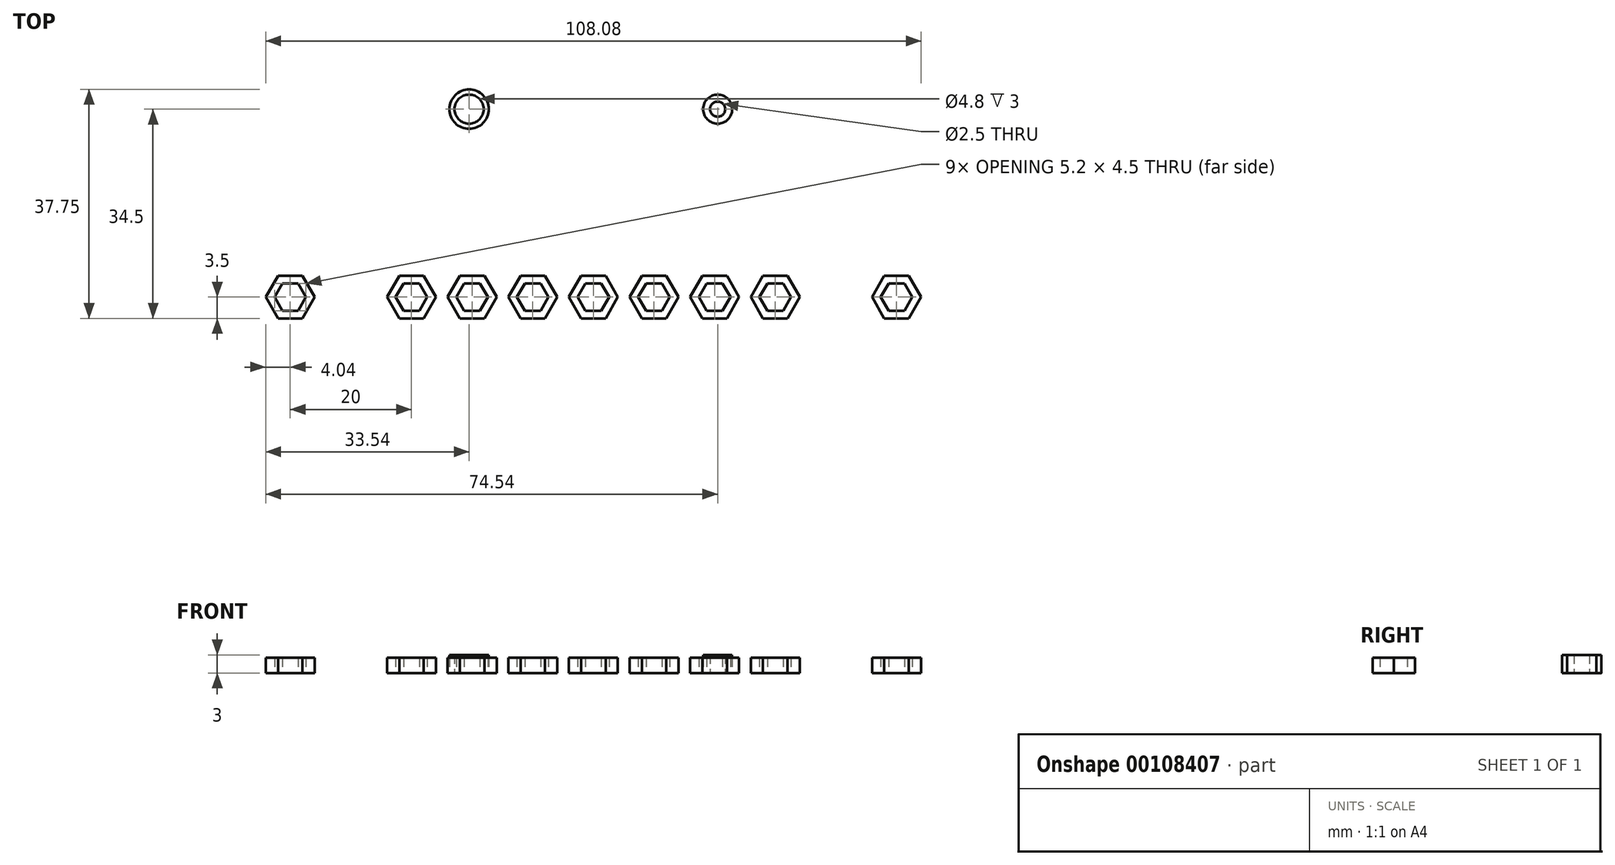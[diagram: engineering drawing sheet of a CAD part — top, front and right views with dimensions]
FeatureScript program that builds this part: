
annotation { "Feature Type Name" : "Feature", "Feature Type Description" : "" }
export const myFeature = defineFeature(function(context is Context, id is Id, definition is map)
    precondition{}
    {
        {
            var Q0;
            Q0=qCreatedBy(makeId("Top.planeOp"),FACE);
            var sketch = newSketch(context, id + "F0", { "sketchPlane" : qUnion([Q0])});
            skLineSegment(sketch, "E0.bottom", {"start": v(-57, 22.5) * mm, "end": v(57, 22.5) * mm});
            skLineSegment(sketch, "E0.top", {"start": v(-57, -22.5) * mm, "end": v(57, -22.5) * mm});
            skLineSegment(sketch, "E0.left", {"start": v(-57, 22.5) * mm, "end": v(-57, -22.5) * mm});
            skLineSegment(sketch, "E0.right", {"start": v(57, 22.5) * mm, "end": v(57, -22.5) * mm});
            skPoint(sketch, "E0.middle", {"position": v(0, 0) * mm});
            skLineSegment(sketch, "E1", {"start": v(57, -22.5) * mm, "end": v(57, -12.5) * mm});
            skLineSegment(sketch, "E2", {"start": v(-57, -22.5) * mm, "end": v(-57, -12.5) * mm});
            skLineSegment(sketch, "E3", {"start": v(0, -22.5) * mm, "end": v(0, -16) * mm});
            skCircle(sketch, "E4.cCircle", {"center": v(0, -16) * mm, "radius": 3.5 * mm, "construction": true});
            skLineSegment(sketch, "E4.0", {"start": v(-2.02, -12.5) * mm, "end": v(2.02, -12.5) * mm});
            skLineSegment(sketch, "E4.1", {"start": v(2.02, -12.5) * mm, "end": v(4.04, -16) * mm});
            skLineSegment(sketch, "E4.2", {"start": v(4.04, -16) * mm, "end": v(2.02, -19.5) * mm});
            skLineSegment(sketch, "E4.3", {"start": v(2.02, -19.5) * mm, "end": v(-2.02, -19.5) * mm});
            skLineSegment(sketch, "E4.4", {"start": v(-2.02, -19.5) * mm, "end": v(-4.04, -16) * mm});
            skLineSegment(sketch, "E4.5", {"start": v(-4.04, -16) * mm, "end": v(-2.02, -12.5) * mm});
            skPoint(sketch, "E4.0.midPoint", {"position": v(0, -12.5) * mm});
            skLineSegment(sketch, "E5", {"start": v(0, -19.5) * mm, "end": v(0, -18.25) * mm});
            skCircle(sketch, "E6.cCircle", {"center": v(0, -16) * mm, "radius": 2.25 * mm, "construction": true});
            skLineSegment(sketch, "E6.0", {"start": v(1.3, -18.25) * mm, "end": v(-1.3, -18.25) * mm});
            skLineSegment(sketch, "E6.1", {"start": v(-1.3, -18.25) * mm, "end": v(-2.6, -16) * mm});
            skLineSegment(sketch, "E6.2", {"start": v(-2.6, -16) * mm, "end": v(-1.3, -13.75) * mm});
            skLineSegment(sketch, "E6.3", {"start": v(-1.3, -13.75) * mm, "end": v(1.3, -13.75) * mm});
            skLineSegment(sketch, "E6.4", {"start": v(1.3, -13.75) * mm, "end": v(2.6, -16) * mm});
            skLineSegment(sketch, "E6.5", {"start": v(2.6, -16) * mm, "end": v(1.3, -18.25) * mm});
            skPoint(sketch, "E6.0.midPoint", {"position": v(0, -18.25) * mm});
            skCircle(sketch, "E7", {"center": v(0, -16) * mm, "radius": 1.5 * mm});
            skLineSegment(sketch, "E8.1.0.0", {"start": v(-5.96, -16) * mm, "end": v(-7.98, -19.5) * mm});
            skLineSegment(sketch, "E8.1.0.1", {"start": v(-7.98, -19.5) * mm, "end": v(-12.02, -19.5) * mm});
            skLineSegment(sketch, "E8.1.0.2", {"start": v(-12.02, -19.5) * mm, "end": v(-14.04, -16) * mm});
            skLineSegment(sketch, "E8.1.0.3", {"start": v(-14.04, -16) * mm, "end": v(-12.02, -12.5) * mm});
            skLineSegment(sketch, "E8.1.0.4", {"start": v(-12.02, -12.5) * mm, "end": v(-7.98, -12.5) * mm});
            skLineSegment(sketch, "E8.1.0.5", {"start": v(-7.98, -12.5) * mm, "end": v(-5.96, -16) * mm});
            skCircle(sketch, "E8.1.0.6", {"center": v(-10, -16) * mm, "radius": 3.5 * mm, "construction": true});
            skLineSegment(sketch, "E8.1.0.7", {"start": v(-11.3, -13.75) * mm, "end": v(-8.7, -13.75) * mm});
            skLineSegment(sketch, "E8.1.0.8", {"start": v(-8.7, -13.75) * mm, "end": v(-7.4, -16) * mm});
            skLineSegment(sketch, "E8.1.0.9", {"start": v(-7.4, -16) * mm, "end": v(-8.7, -18.25) * mm});
            skLineSegment(sketch, "E8.1.0.10", {"start": v(-8.7, -18.25) * mm, "end": v(-11.3, -18.25) * mm});
            skLineSegment(sketch, "E8.1.0.11", {"start": v(-11.3, -18.25) * mm, "end": v(-12.6, -16) * mm});
            skLineSegment(sketch, "E8.1.0.12", {"start": v(-12.6, -16) * mm, "end": v(-11.3, -13.75) * mm});
            skCircle(sketch, "E8.1.0.13", {"center": v(-10, -16) * mm, "radius": 2.25 * mm, "construction": true});
            skCircle(sketch, "E8.1.0.14", {"center": v(-10, -16) * mm, "radius": 1.5 * mm});
            skLineSegment(sketch, "E8.2.0.0", {"start": v(-15.96, -16) * mm, "end": v(-17.98, -19.5) * mm});
            skLineSegment(sketch, "E8.2.0.1", {"start": v(-17.98, -19.5) * mm, "end": v(-22.02, -19.5) * mm});
            skLineSegment(sketch, "E8.2.0.2", {"start": v(-22.02, -19.5) * mm, "end": v(-24.04, -16) * mm});
            skLineSegment(sketch, "E8.2.0.3", {"start": v(-24.04, -16) * mm, "end": v(-22.02, -12.5) * mm});
            skLineSegment(sketch, "E8.2.0.4", {"start": v(-22.02, -12.5) * mm, "end": v(-17.98, -12.5) * mm});
            skLineSegment(sketch, "E8.2.0.5", {"start": v(-17.98, -12.5) * mm, "end": v(-15.96, -16) * mm});
            skCircle(sketch, "E8.2.0.6", {"center": v(-20, -16) * mm, "radius": 3.5 * mm, "construction": true});
            skLineSegment(sketch, "E8.2.0.7", {"start": v(-21.3, -13.75) * mm, "end": v(-18.7, -13.75) * mm});
            skLineSegment(sketch, "E8.2.0.8", {"start": v(-18.7, -13.75) * mm, "end": v(-17.4, -16) * mm});
            skLineSegment(sketch, "E8.2.0.9", {"start": v(-17.4, -16) * mm, "end": v(-18.7, -18.25) * mm});
            skLineSegment(sketch, "E8.2.0.10", {"start": v(-18.7, -18.25) * mm, "end": v(-21.3, -18.25) * mm});
            skLineSegment(sketch, "E8.2.0.11", {"start": v(-21.3, -18.25) * mm, "end": v(-22.6, -16) * mm});
            skLineSegment(sketch, "E8.2.0.12", {"start": v(-22.6, -16) * mm, "end": v(-21.3, -13.75) * mm});
            skCircle(sketch, "E8.2.0.13", {"center": v(-20, -16) * mm, "radius": 2.25 * mm, "construction": true});
            skCircle(sketch, "E8.2.0.14", {"center": v(-20, -16) * mm, "radius": 1.5 * mm});
            skLineSegment(sketch, "E8.3.0.0", {"start": v(-25.96, -16) * mm, "end": v(-27.98, -19.5) * mm});
            skLineSegment(sketch, "E8.3.0.1", {"start": v(-27.98, -19.5) * mm, "end": v(-32.02, -19.5) * mm});
            skLineSegment(sketch, "E8.3.0.2", {"start": v(-32.02, -19.5) * mm, "end": v(-34.04, -16) * mm});
            skLineSegment(sketch, "E8.3.0.3", {"start": v(-34.04, -16) * mm, "end": v(-32.02, -12.5) * mm});
            skLineSegment(sketch, "E8.3.0.4", {"start": v(-32.02, -12.5) * mm, "end": v(-27.98, -12.5) * mm});
            skLineSegment(sketch, "E8.3.0.5", {"start": v(-27.98, -12.5) * mm, "end": v(-25.96, -16) * mm});
            skCircle(sketch, "E8.3.0.6", {"center": v(-30, -16) * mm, "radius": 3.5 * mm, "construction": true});
            skLineSegment(sketch, "E8.3.0.7", {"start": v(-31.3, -13.75) * mm, "end": v(-28.7, -13.75) * mm});
            skLineSegment(sketch, "E8.3.0.8", {"start": v(-28.7, -13.75) * mm, "end": v(-27.4, -16) * mm});
            skLineSegment(sketch, "E8.3.0.9", {"start": v(-27.4, -16) * mm, "end": v(-28.7, -18.25) * mm});
            skLineSegment(sketch, "E8.3.0.10", {"start": v(-28.7, -18.25) * mm, "end": v(-31.3, -18.25) * mm});
            skLineSegment(sketch, "E8.3.0.11", {"start": v(-31.3, -18.25) * mm, "end": v(-32.6, -16) * mm});
            skLineSegment(sketch, "E8.3.0.12", {"start": v(-32.6, -16) * mm, "end": v(-31.3, -13.75) * mm});
            skCircle(sketch, "E8.3.0.13", {"center": v(-30, -16) * mm, "radius": 2.25 * mm, "construction": true});
            skCircle(sketch, "E8.3.0.14", {"center": v(-30, -16) * mm, "radius": 1.5 * mm});
            skCircle(sketch, "E8.4.0.14", {"center": v(-40, -16) * mm, "radius": 1.5 * mm});
            skLineSegment(sketch, "E8.5.0.0", {"start": v(-45.96, -16) * mm, "end": v(-47.98, -19.5) * mm});
            skLineSegment(sketch, "E8.5.0.1", {"start": v(-47.98, -19.5) * mm, "end": v(-52.02, -19.5) * mm});
            skLineSegment(sketch, "E8.5.0.2", {"start": v(-52.02, -19.5) * mm, "end": v(-54.04, -16) * mm});
            skLineSegment(sketch, "E8.5.0.3", {"start": v(-54.04, -16) * mm, "end": v(-52.02, -12.5) * mm});
            skLineSegment(sketch, "E8.5.0.4", {"start": v(-52.02, -12.5) * mm, "end": v(-47.98, -12.5) * mm});
            skLineSegment(sketch, "E8.5.0.5", {"start": v(-47.98, -12.5) * mm, "end": v(-45.96, -16) * mm});
            skCircle(sketch, "E8.5.0.6", {"center": v(-50, -16) * mm, "radius": 3.5 * mm, "construction": true});
            skLineSegment(sketch, "E8.5.0.7", {"start": v(-51.3, -13.75) * mm, "end": v(-48.7, -13.75) * mm});
            skLineSegment(sketch, "E8.5.0.8", {"start": v(-48.7, -13.75) * mm, "end": v(-47.4, -16) * mm});
            skLineSegment(sketch, "E8.5.0.9", {"start": v(-47.4, -16) * mm, "end": v(-48.7, -18.25) * mm});
            skLineSegment(sketch, "E8.5.0.10", {"start": v(-48.7, -18.25) * mm, "end": v(-51.3, -18.25) * mm});
            skLineSegment(sketch, "E8.5.0.11", {"start": v(-51.3, -18.25) * mm, "end": v(-52.6, -16) * mm});
            skLineSegment(sketch, "E8.5.0.12", {"start": v(-52.6, -16) * mm, "end": v(-51.3, -13.75) * mm});
            skCircle(sketch, "E8.5.0.13", {"center": v(-50, -16) * mm, "radius": 2.25 * mm, "construction": true});
            skCircle(sketch, "E8.5.0.14", {"center": v(-50, -16) * mm, "radius": 1.5 * mm});
            skLineSegment(sketch, "E8.direction1", {"start": v(-2.02, -19.5) * mm, "end": v(-12.02, -19.5) * mm, "construction": true});
            skLineSegment(sketch, "E9.1.0.0", {"start": v(7.98, -12.5) * mm, "end": v(12.02, -12.5) * mm});
            skLineSegment(sketch, "E9.1.0.1", {"start": v(12.02, -12.5) * mm, "end": v(14.04, -16) * mm});
            skLineSegment(sketch, "E9.1.0.2", {"start": v(14.04, -16) * mm, "end": v(12.02, -19.5) * mm});
            skLineSegment(sketch, "E9.1.0.3", {"start": v(12.02, -19.5) * mm, "end": v(7.98, -19.5) * mm});
            skLineSegment(sketch, "E9.1.0.4", {"start": v(7.98, -19.5) * mm, "end": v(5.96, -16) * mm});
            skLineSegment(sketch, "E9.1.0.5", {"start": v(5.96, -16) * mm, "end": v(7.98, -12.5) * mm});
            skLineSegment(sketch, "E9.1.0.6", {"start": v(8.7, -13.75) * mm, "end": v(11.3, -13.75) * mm});
            skLineSegment(sketch, "E9.1.0.7", {"start": v(7.4, -16) * mm, "end": v(8.7, -13.75) * mm});
            skCircle(sketch, "E9.1.0.8", {"center": v(10, -16) * mm, "radius": 2.25 * mm, "construction": true});
            skLineSegment(sketch, "E9.1.0.9", {"start": v(11.3, -13.75) * mm, "end": v(12.6, -16) * mm});
            skLineSegment(sketch, "E9.1.0.10", {"start": v(12.6, -16) * mm, "end": v(11.3, -18.25) * mm});
            skLineSegment(sketch, "E9.1.0.11", {"start": v(11.3, -18.25) * mm, "end": v(8.7, -18.25) * mm});
            skLineSegment(sketch, "E9.1.0.12", {"start": v(8.7, -18.25) * mm, "end": v(7.4, -16) * mm});
            skCircle(sketch, "E9.1.0.13", {"center": v(10, -16) * mm, "radius": 3.5 * mm, "construction": true});
            skCircle(sketch, "E9.1.0.14", {"center": v(10, -16) * mm, "radius": 1.5 * mm});
            skLineSegment(sketch, "E9.2.0.0", {"start": v(17.98, -12.5) * mm, "end": v(22.02, -12.5) * mm});
            skLineSegment(sketch, "E9.2.0.1", {"start": v(22.02, -12.5) * mm, "end": v(24.04, -16) * mm});
            skLineSegment(sketch, "E9.2.0.2", {"start": v(24.04, -16) * mm, "end": v(22.02, -19.5) * mm});
            skLineSegment(sketch, "E9.2.0.3", {"start": v(22.02, -19.5) * mm, "end": v(17.98, -19.5) * mm});
            skLineSegment(sketch, "E9.2.0.4", {"start": v(17.98, -19.5) * mm, "end": v(15.96, -16) * mm});
            skLineSegment(sketch, "E9.2.0.5", {"start": v(15.96, -16) * mm, "end": v(17.98, -12.5) * mm});
            skLineSegment(sketch, "E9.2.0.6", {"start": v(18.7, -13.75) * mm, "end": v(21.3, -13.75) * mm});
            skLineSegment(sketch, "E9.2.0.7", {"start": v(17.4, -16) * mm, "end": v(18.7, -13.75) * mm});
            skCircle(sketch, "E9.2.0.8", {"center": v(20, -16) * mm, "radius": 2.25 * mm, "construction": true});
            skLineSegment(sketch, "E9.2.0.9", {"start": v(21.3, -13.75) * mm, "end": v(22.6, -16) * mm});
            skLineSegment(sketch, "E9.2.0.10", {"start": v(22.6, -16) * mm, "end": v(21.3, -18.25) * mm});
            skLineSegment(sketch, "E9.2.0.11", {"start": v(21.3, -18.25) * mm, "end": v(18.7, -18.25) * mm});
            skLineSegment(sketch, "E9.2.0.12", {"start": v(18.7, -18.25) * mm, "end": v(17.4, -16) * mm});
            skCircle(sketch, "E9.2.0.13", {"center": v(20, -16) * mm, "radius": 3.5 * mm, "construction": true});
            skCircle(sketch, "E9.2.0.14", {"center": v(20, -16) * mm, "radius": 1.5 * mm});
            skLineSegment(sketch, "E9.3.0.0", {"start": v(27.98, -12.5) * mm, "end": v(32.02, -12.5) * mm});
            skLineSegment(sketch, "E9.3.0.1", {"start": v(32.02, -12.5) * mm, "end": v(34.04, -16) * mm});
            skLineSegment(sketch, "E9.3.0.2", {"start": v(34.04, -16) * mm, "end": v(32.02, -19.5) * mm});
            skLineSegment(sketch, "E9.3.0.3", {"start": v(32.02, -19.5) * mm, "end": v(27.98, -19.5) * mm});
            skLineSegment(sketch, "E9.3.0.4", {"start": v(27.98, -19.5) * mm, "end": v(25.96, -16) * mm});
            skLineSegment(sketch, "E9.3.0.5", {"start": v(25.96, -16) * mm, "end": v(27.98, -12.5) * mm});
            skLineSegment(sketch, "E9.3.0.6", {"start": v(28.7, -13.75) * mm, "end": v(31.3, -13.75) * mm});
            skLineSegment(sketch, "E9.3.0.7", {"start": v(27.4, -16) * mm, "end": v(28.7, -13.75) * mm});
            skCircle(sketch, "E9.3.0.8", {"center": v(30, -16) * mm, "radius": 2.25 * mm, "construction": true});
            skLineSegment(sketch, "E9.3.0.9", {"start": v(31.3, -13.75) * mm, "end": v(32.6, -16) * mm});
            skLineSegment(sketch, "E9.3.0.10", {"start": v(32.6, -16) * mm, "end": v(31.3, -18.25) * mm});
            skLineSegment(sketch, "E9.3.0.11", {"start": v(31.3, -18.25) * mm, "end": v(28.7, -18.25) * mm});
            skLineSegment(sketch, "E9.3.0.12", {"start": v(28.7, -18.25) * mm, "end": v(27.4, -16) * mm});
            skCircle(sketch, "E9.3.0.13", {"center": v(30, -16) * mm, "radius": 3.5 * mm, "construction": true});
            skCircle(sketch, "E9.3.0.14", {"center": v(30, -16) * mm, "radius": 1.5 * mm});
            skCircle(sketch, "E9.4.0.14", {"center": v(40, -16) * mm, "radius": 1.5 * mm});
            skLineSegment(sketch, "E9.5.0.0", {"start": v(47.98, -12.5) * mm, "end": v(52.02, -12.5) * mm});
            skLineSegment(sketch, "E9.5.0.1", {"start": v(52.02, -12.5) * mm, "end": v(54.04, -16) * mm});
            skLineSegment(sketch, "E9.5.0.2", {"start": v(54.04, -16) * mm, "end": v(52.02, -19.5) * mm});
            skLineSegment(sketch, "E9.5.0.3", {"start": v(52.02, -19.5) * mm, "end": v(47.98, -19.5) * mm});
            skLineSegment(sketch, "E9.5.0.4", {"start": v(47.98, -19.5) * mm, "end": v(45.96, -16) * mm});
            skLineSegment(sketch, "E9.5.0.5", {"start": v(45.96, -16) * mm, "end": v(47.98, -12.5) * mm});
            skLineSegment(sketch, "E9.5.0.6", {"start": v(48.7, -13.75) * mm, "end": v(51.3, -13.75) * mm});
            skLineSegment(sketch, "E9.5.0.7", {"start": v(47.4, -16) * mm, "end": v(48.7, -13.75) * mm});
            skCircle(sketch, "E9.5.0.8", {"center": v(50, -16) * mm, "radius": 2.25 * mm, "construction": true});
            skLineSegment(sketch, "E9.5.0.9", {"start": v(51.3, -13.75) * mm, "end": v(52.6, -16) * mm});
            skLineSegment(sketch, "E9.5.0.10", {"start": v(52.6, -16) * mm, "end": v(51.3, -18.25) * mm});
            skLineSegment(sketch, "E9.5.0.11", {"start": v(51.3, -18.25) * mm, "end": v(48.7, -18.25) * mm});
            skLineSegment(sketch, "E9.5.0.12", {"start": v(48.7, -18.25) * mm, "end": v(47.4, -16) * mm});
            skCircle(sketch, "E9.5.0.13", {"center": v(50, -16) * mm, "radius": 3.5 * mm, "construction": true});
            skCircle(sketch, "E9.5.0.14", {"center": v(50, -16) * mm, "radius": 1.5 * mm});
            skLineSegment(sketch, "E9.direction1", {"start": v(-2.02, -19.5) * mm, "end": v(7.98, -19.5) * mm, "construction": true});
            skLineSegment(sketch, "E10", {"start": v(-57, -12.5) * mm, "end": v(57, -12.5) * mm});
            skLineSegment(sketch, "E11", {"start": v(0, -22.5) * mm, "end": v(0, 5.5) * mm});
            skCircle(sketch, "E12", {"center": v(0, 5.5) * mm, "radius": 2.5 * mm});
            skLineSegment(sketch, "E13", {"start": v(0, 0) * mm, "end": v(0, 8) * mm});
            skLineSegment(sketch, "E14", {"start": v(0, 8) * mm, "end": v(0, 10) * mm});
            skLineSegment(sketch, "E15", {"start": v(0, 10) * mm, "end": v(-2, 10) * mm});
            skLineSegment(sketch, "E16", {"start": v(0, 10) * mm, "end": v(2, 10) * mm});
            skLineSegment(sketch, "E17", {"start": v(-2, 10) * mm, "end": v(-2, 16.5) * mm});
            skLineSegment(sketch, "E18", {"start": v(2, 10) * mm, "end": v(2, 16.5) * mm});
            skLineSegment(sketch, "E19", {"start": v(2, 16.5) * mm, "end": v(-2, 16.5) * mm});
            skLineSegment(sketch, "E20", {"start": v(-2, 10) * mm, "end": v(-9.5, 10) * mm});
            skLineSegment(sketch, "E21.1.0.0", {"start": v(9.5, 16.5) * mm, "end": v(5.5, 16.5) * mm});
            skLineSegment(sketch, "E21.1.0.1", {"start": v(5.5, 10) * mm, "end": v(5.5, 16.5) * mm});
            skLineSegment(sketch, "E21.1.0.2", {"start": v(9.5, 10) * mm, "end": v(9.5, 16.5) * mm});
            skLineSegment(sketch, "E21.1.0.3", {"start": v(7.5, 10) * mm, "end": v(9.5, 10) * mm});
            skLineSegment(sketch, "E21.1.0.4", {"start": v(7.5, 10) * mm, "end": v(5.5, 10) * mm});
            skLineSegment(sketch, "E21.2.0.0", {"start": v(17, 16.5) * mm, "end": v(13, 16.5) * mm});
            skLineSegment(sketch, "E21.2.0.1", {"start": v(13, 10) * mm, "end": v(13, 16.5) * mm});
            skLineSegment(sketch, "E21.2.0.2", {"start": v(17, 10) * mm, "end": v(17, 16.5) * mm});
            skLineSegment(sketch, "E21.2.0.3", {"start": v(15, 10) * mm, "end": v(17, 10) * mm});
            skLineSegment(sketch, "E21.2.0.4", {"start": v(15, 10) * mm, "end": v(13, 10) * mm});
            skLineSegment(sketch, "E22.1.0.0", {"start": v(-5.5, 10) * mm, "end": v(-5.5, 16.5) * mm});
            skLineSegment(sketch, "E22.1.0.1", {"start": v(-9.5, 10) * mm, "end": v(-9.5, 16.5) * mm});
            skLineSegment(sketch, "E22.1.0.2", {"start": v(-7.5, 10) * mm, "end": v(-9.5, 10) * mm});
            skLineSegment(sketch, "E22.1.0.3", {"start": v(-7.5, 10) * mm, "end": v(-5.5, 10) * mm});
            skLineSegment(sketch, "E22.1.0.4", {"start": v(-5.5, 16.5) * mm, "end": v(-9.5, 16.5) * mm});
            skLineSegment(sketch, "E22.2.0.0", {"start": v(-13, 10) * mm, "end": v(-13, 16.5) * mm});
            skLineSegment(sketch, "E22.2.0.1", {"start": v(-17, 10) * mm, "end": v(-17, 16.5) * mm});
            skLineSegment(sketch, "E22.2.0.2", {"start": v(-15, 10) * mm, "end": v(-17, 10) * mm});
            skLineSegment(sketch, "E22.2.0.3", {"start": v(-15, 10) * mm, "end": v(-13, 10) * mm});
            skLineSegment(sketch, "E22.2.0.4", {"start": v(-13, 16.5) * mm, "end": v(-17, 16.5) * mm});
            skLineSegment(sketch, "E22.direction1", {"start": v(-2, 10) * mm, "end": v(-9.5, 10) * mm, "construction": true});
            skLineSegment(sketch, "E23", {"start": v(2, 10) * mm, "end": v(9.5, 10) * mm, "construction": true});
            skLineSegment(sketch, "E24", {"start": v(20.25, 15) * mm, "end": v(20.25, 22.5) * mm});
            skLineSegment(sketch, "E25", {"start": v(-20.5, 15) * mm, "end": v(-20.5, 22.5) * mm});
            skLineSegment(sketch, "E26", {"start": v(-52.5, 22.5) * mm, "end": v(-52.5, 19) * mm});
            skLineSegment(sketch, "E27.bottom", {"start": v(-52.5, 19) * mm, "end": v(-48, 19) * mm});
            skLineSegment(sketch, "E27.top", {"start": v(-52.5, 12) * mm, "end": v(-48, 12) * mm});
            skLineSegment(sketch, "E27.left", {"start": v(-52.5, 19) * mm, "end": v(-52.5, 12) * mm});
            skLineSegment(sketch, "E27.right", {"start": v(-48, 19) * mm, "end": v(-48, 12) * mm});
            skLineSegment(sketch, "E28.MirrorCS", {"start": v(52.5, 12) * mm, "end": v(48, 12) * mm});
            skLineSegment(sketch, "E29.MirrorCS", {"start": v(48, 19) * mm, "end": v(48, 12) * mm});
            skLineSegment(sketch, "E30.MirrorCS", {"start": v(52.5, 19) * mm, "end": v(52.5, 12) * mm});
            skLineSegment(sketch, "E31.MirrorCS", {"start": v(52.5, 19) * mm, "end": v(48, 19) * mm});
            skCircle(sketch, "E32", {"center": v(-20.5, 15) * mm, "radius": 1.25 * mm});
            skCircle(sketch, "E33", {"center": v(-20.5, 15) * mm, "radius": 2.4 * mm});
            skCircle(sketch, "E34", {"center": v(-20.5, 15) * mm, "radius": 3.25 * mm});
            skCircle(sketch, "E35.MirrorC", {"center": v(20.5, 15) * mm, "radius": 1.25 * mm});
            skCircle(sketch, "E36.MirrorC", {"center": v(20.5, 15) * mm, "radius": 2.4 * mm});
            skCircle(sketch, "E37.MirrorC", {"center": v(20.5, 15) * mm, "radius": 3.25 * mm});
            skLineSegment(sketch, "E38", {"start": v(0, 22.5) * mm, "end": v(-57, 22.5) * mm});
            skSolve(sketch);
        }
        {
            var Q0;
            {var subQ0=sQuery(id+"F0.wireOp",EDGE,"E9.2.0.1");Q0=makeQuery(id+"F0.imprint","IMPRINT",FACE,{"disambiguationData":[TD([[makeQuery(id+"F0.imprint","IMPRINT",EDGE,{"derivedFrom":subQ0}),-1.0]])]});}
            var Q1;
            {var subQ1=sQuery(id+"F0.wireOp",EDGE,"E9.1.0.1");Q1=makeQuery(id+"F0.imprint","IMPRINT",FACE,{"disambiguationData":[TD([[makeQuery(id+"F0.imprint","IMPRINT",EDGE,{"derivedFrom":subQ1}),-1.0]])]});}
            var Q2;
            {var subQ11=sQuery(id+"F0.wireOp",EDGE,"E4.1");Q2=makeQuery(id+"F0.imprint","IMPRINT",FACE,{"disambiguationData":[TD([[makeQuery(id+"F0.imprint","IMPRINT",EDGE,{"derivedFrom":subQ11}),-1.0]])]});}
            var Q3;
            {var subQ4=sQuery(id+"F0.wireOp",EDGE,"E4.4");Q3=makeQuery(id+"F0.imprint","IMPRINT",FACE,{"disambiguationData":[TD([[makeQuery(id+"F0.imprint","IMPRINT",EDGE,{"derivedFrom":subQ4}),-1.0]])]});}
            var Q4;
            Q4=makeQuery(id+"F0.imprint","IMPRINT",FACE,{"disambiguationData":[TD([[makeQuery(id+"F0.imprint","IMPRINT",EDGE,{"derivedFrom":sQuery(id+"F0.wireOp",EDGE,"E8.1.0.0")}),-1.0]])]});
            var Q5;
            Q5=makeQuery(id+"F0.imprint","IMPRINT",FACE,{"disambiguationData":[TD([[makeQuery(id+"F0.imprint","IMPRINT",EDGE,{"derivedFrom":sQuery(id+"F0.wireOp",EDGE,"E8.2.0.0")}),-1.0]])]});
            var Q6;
            Q6=makeQuery(id+"F0.imprint","IMPRINT",FACE,{"disambiguationData":[TD([[makeQuery(id+"F0.imprint","IMPRINT",EDGE,{"derivedFrom":sQuery(id+"F0.wireOp",EDGE,"E8.3.0.0")}),-1.0]])]});
            var Q7;
            Q7=makeQuery(id+"F0.imprint","IMPRINT",FACE,{"disambiguationData":[TD([[makeQuery(id+"F0.imprint","IMPRINT",EDGE,{"derivedFrom":sQuery(id+"F0.wireOp",EDGE,"E8.5.0.0")}),-1.0]])]});
            var Q8;
            {var subQ1=sQuery(id+"F0.wireOp",EDGE,"E9.5.0.1");Q8=makeQuery(id+"F0.imprint","IMPRINT",FACE,{"disambiguationData":[TD([[makeQuery(id+"F0.imprint","IMPRINT",EDGE,{"derivedFrom":subQ1}),-1.0]])]});}
            var Q9;
            {var subQ1=sQuery(id+"F0.wireOp",EDGE,"E9.3.0.1");Q9=makeQuery(id+"F0.imprint","IMPRINT",FACE,{"disambiguationData":[TD([[makeQuery(id+"F0.imprint","IMPRINT",EDGE,{"derivedFrom":subQ1}),-1.0]])]});}
            extrude(context, id + "F1", {"entities" : qUnion([Q0, Q1, Q2, Q3, Q4, Q5, Q6, Q7, Q8, Q9]), "depth" : 2.5 * mm});
        }
        {
            var Q0;
            Q0=makeQuery(id+"F0.imprint","IMPRINT",FACE,{"disambiguationData":[TD([[makeQuery(id+"F0.imprint","IMPRINT",EDGE,{"derivedFrom":sQuery(id+"F0.wireOp",EDGE,"E33")}),-1.0]])]});
            var Q1;
            Q1=makeQuery(id+"F0.imprint","IMPRINT",FACE,{"disambiguationData":[TD([[makeQuery(id+"F0.imprint","IMPRINT",EDGE,{"derivedFrom":sQuery(id+"F0.wireOp",EDGE,"E36.MirrorC")}),1.0]])]});
            extrude(context, id + "F2", {"entities" : qUnion([Q0, Q1]), "depth" : 3 * mm});
        }
    });
